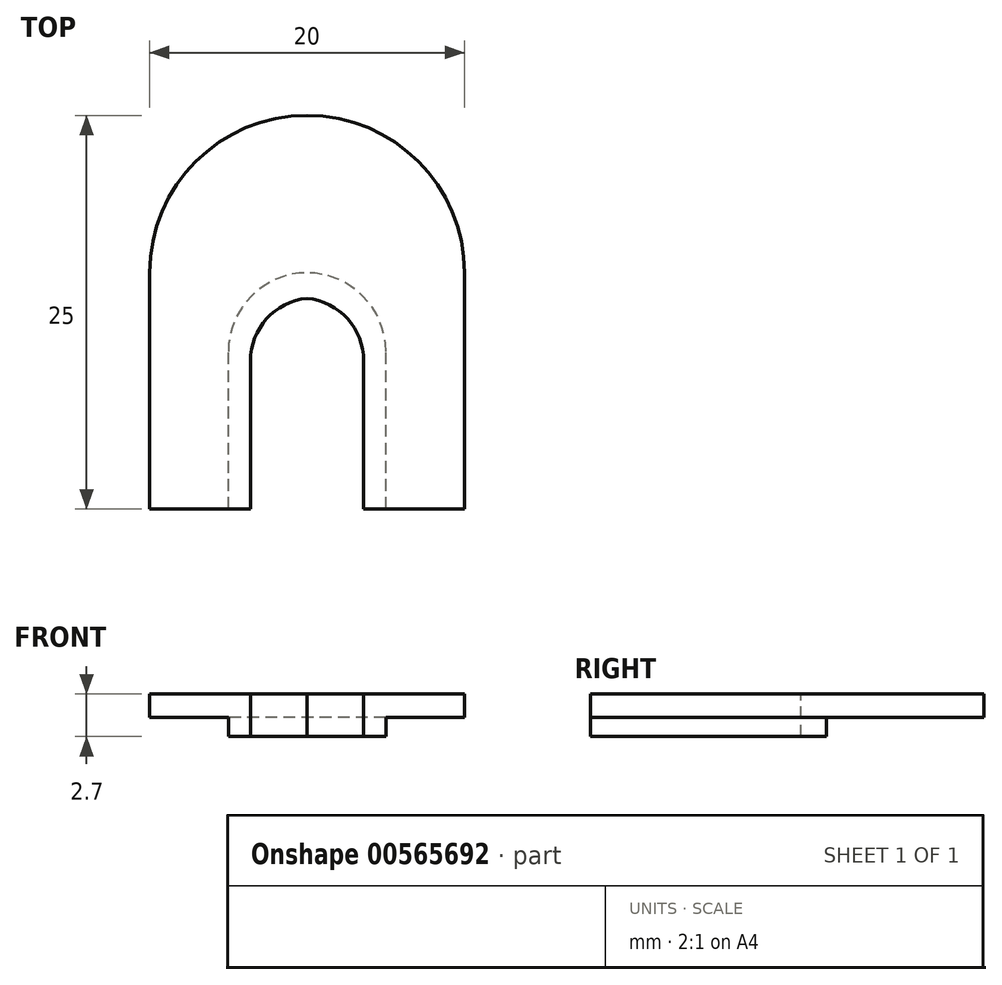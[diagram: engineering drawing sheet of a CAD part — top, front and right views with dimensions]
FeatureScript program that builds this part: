
annotation { "Feature Type Name" : "Feature", "Feature Type Description" : "" }
export const myFeature = defineFeature(function(context is Context, id is Id, definition is map)
    precondition{}
    {
        {
            var Q0;
            Q0=qCreatedBy(makeId("Top.planeOp"),FACE);
            var sketch = newSketch(context, id + "F0", { "sketchPlane" : qUnion([Q0])});
            skLineSegment(sketch, "E0", {"start": v(-3.6, 0) * mm, "end": v(-10, 0) * mm});
            skLineSegment(sketch, "E1", {"start": v(-10, 0) * mm, "end": v(-10, 25) * mm});
            skLineSegment(sketch, "E2", {"start": v(-10, 25) * mm, "end": v(0, 25) * mm});
            skLineSegment(sketch, "E3", {"start": v(0, 13.4) * mm, "end": v(-3.6, 13.4) * mm});
            skLineSegment(sketch, "E4", {"start": v(-3.6, 13.4) * mm, "end": v(-3.6, 0) * mm});
            skLineSegment(sketch, "E5", {"start": v(0, 0) * mm, "end": v(0, -8.86) * mm, "construction": true});
            skLineSegment(sketch, "E6.MirrorCS", {"start": v(10, 0) * mm, "end": v(10, 25) * mm});
            skLineSegment(sketch, "E7.MirrorCS", {"start": v(0, 13.4) * mm, "end": v(3.6, 13.4) * mm});
            skLineSegment(sketch, "E8.MirrorCS", {"start": v(10, 25) * mm, "end": v(0, 25) * mm});
            skLineSegment(sketch, "E9.MirrorCS", {"start": v(3.6, 0) * mm, "end": v(10, 0) * mm});
            skLineSegment(sketch, "E10.MirrorCS", {"start": v(3.6, 13.4) * mm, "end": v(3.6, 0) * mm});
            skSolve(sketch);
        }
        {
            var Q0;
            Q0 = qSketchRegion(id + "F0", true);
            extrude(context, id + "F1", {"entities" : qUnion([Q0]), "depth" : 2.7 * mm, "offsetDistance" : 25 * mm});
        }
        {
            var Q0;
            Q0=makeQuery(id+"F1.opExtrude","SWEPT_EDGE",EDGE,{"disambiguationData":[OSD([sQuery(id+"F0.wireOp",EDGE,"E3"),sQuery(id+"F0.wireOp",EDGE,"E4")])]});
            var Q1;
            Q1=makeQuery(id+"F1.opExtrude","SWEPT_EDGE",EDGE,{"disambiguationData":[OSD([sQuery(id+"F0.wireOp",EDGE,"E7.MirrorCS"),sQuery(id+"F0.wireOp",EDGE,"E10.MirrorCS")])]});
            fillet(context, id + "F2", {"entities" : qUnion([Q0, Q1]), "radius" : 4 * mm, "tangentPropagation" : true, "allowEdgeOverflow" : false});
        }
        {
            var Q0;
            Q0=makeQuery(id+"F1.opExtrude","SWEPT_EDGE",EDGE,{"disambiguationData":[OSD([sQuery(id+"F0.wireOp",EDGE,"E1"),sQuery(id+"F0.wireOp",EDGE,"E2")])]});
            var Q1;
            Q1=makeQuery(id+"F1.opExtrude","SWEPT_EDGE",EDGE,{"disambiguationData":[OSD([sQuery(id+"F0.wireOp",EDGE,"E6.MirrorCS"),sQuery(id+"F0.wireOp",EDGE,"E8.MirrorCS")])]});
            fillet(context, id + "F3", {"entities" : qUnion([Q0, Q1]), "radius" : 10 * mm, "tangentPropagation" : true, "allowEdgeOverflow" : false});
        }
        {
            var Q0;
            Q0=qCreatedBy(makeId("Top.planeOp"),FACE);
            var sketch = newSketch(context, id + "F4", { "sketchPlane" : qUnion([Q0])});
            skLineSegment(sketch, "E11", {"start": v(-5, -1.05) * mm, "end": v(-5, 10) * mm});
            skLineSegment(sketch, "E12", {"start": v(0, 15) * mm, "end": v(0, 15) * mm});
            skPoint(sketch, "E13.visualSharp", {"position": v(-5, 15) * mm});
            skArc(sketch, "E13.filletArc", {"start": v(0, 15) * mm, "mid": v(-3.54, 13.54) * mm, "end": v(-5, 10) * mm});
            skLineSegment(sketch, "E14", {"start": v(-5, -1.05) * mm, "end": v(-11.25, -1.05) * mm});
            skLineSegment(sketch, "E15", {"start": v(-11.25, -1.05) * mm, "end": v(-11.25, 27.13) * mm});
            skLineSegment(sketch, "E16", {"start": v(-11.25, 27.13) * mm, "end": v(0, 27.13) * mm});
            skLineSegment(sketch, "E17", {"start": v(0, 23.46) * mm, "end": v(0, 27.13) * mm, "construction": true});
            skLineSegment(sketch, "E18.MirrorCS", {"start": v(5, -1.05) * mm, "end": v(11.25, -1.05) * mm});
            skArc(sketch, "E19.MirrorCS", {"start": v(0, 15) * mm, "mid": v(3.54, 13.54) * mm, "end": v(5, 10) * mm});
            skLineSegment(sketch, "E20.MirrorCS", {"start": v(11.25, 27.13) * mm, "end": v(0, 27.13) * mm});
            skLineSegment(sketch, "E21.MirrorCS", {"start": v(11.25, -1.05) * mm, "end": v(11.25, 27.13) * mm});
            skLineSegment(sketch, "E22.MirrorCS", {"start": v(5, -1.05) * mm, "end": v(5, 10) * mm});
            skPoint(sketch, "E23.MirrorP", {"position": v(5, 15) * mm});
            skSolve(sketch);
        }
        {
            var Q0;
            Q0 = qSketchRegion(id + "F4", true);
            extrude(context, id + "F5", {"entities" : qUnion([Q0]), "operationType" : NewBodyOperationType.REMOVE, "depth" : 1.2 * mm, "offsetDistance" : 25 * mm});
        }
    });
